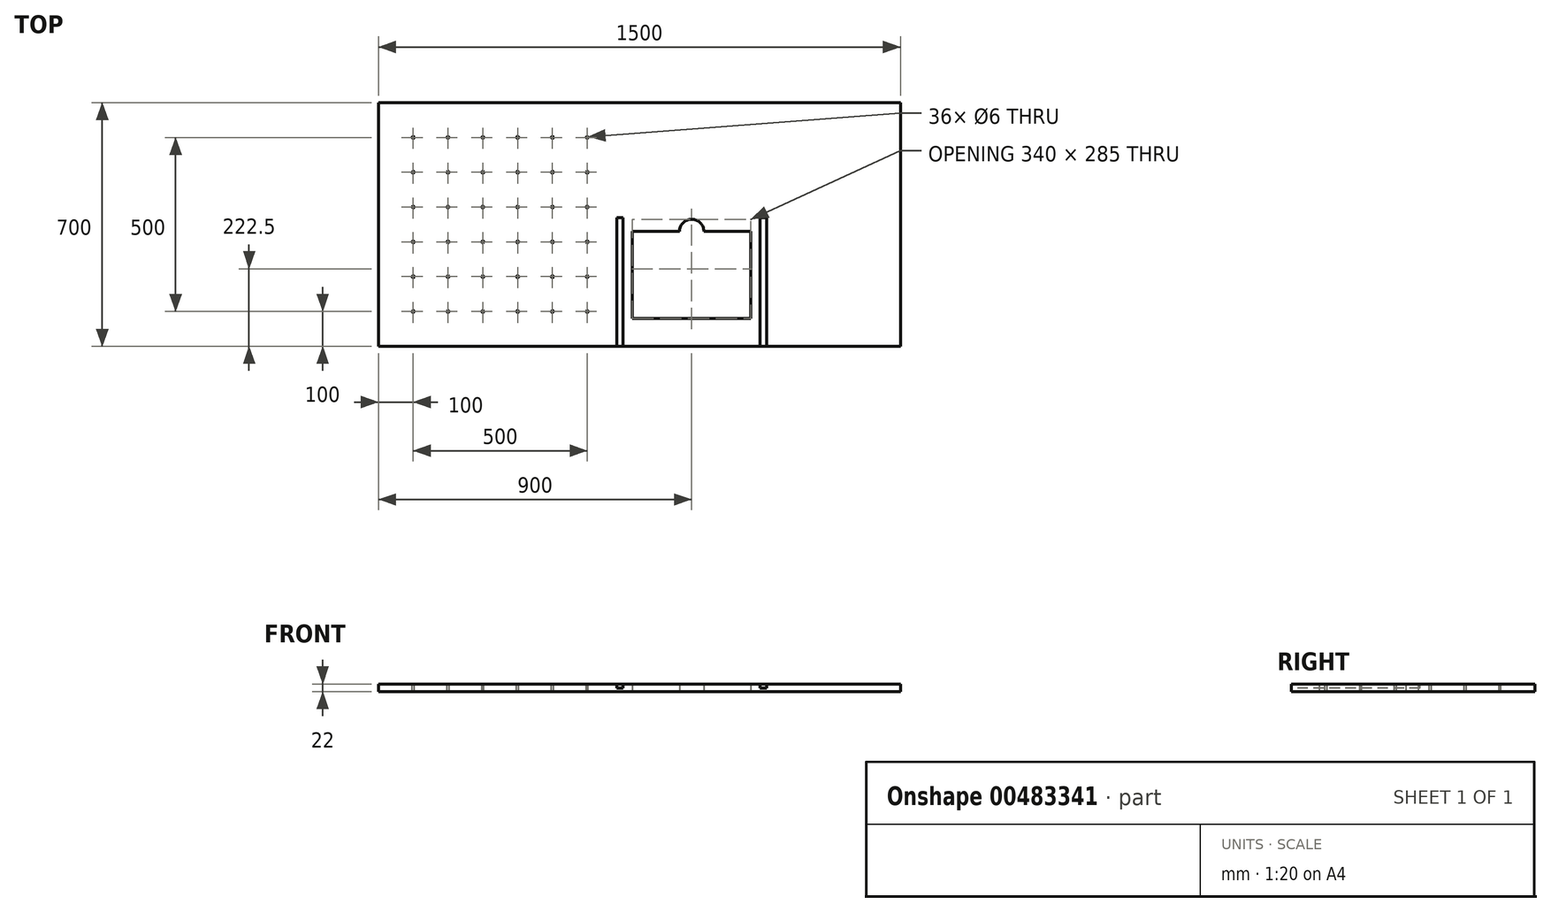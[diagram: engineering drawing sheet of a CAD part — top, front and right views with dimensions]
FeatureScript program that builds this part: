
annotation { "Feature Type Name" : "Feature", "Feature Type Description" : "" }
export const myFeature = defineFeature(function(context is Context, id is Id, definition is map)
    precondition{}
    {
        {
            var Q0;
            Q0=qCreatedBy(makeId("Top.planeOp"),FACE);
            var sketch = newSketch(context, id + "F0", { "sketchPlane" : qUnion([Q0])});
            skLineSegment(sketch, "E0.bottom", {"start": v(750, 350) * mm, "end": v(-750, 350) * mm});
            skLineSegment(sketch, "E0.top", {"start": v(750, -350) * mm, "end": v(-750, -350) * mm});
            skLineSegment(sketch, "E0.left", {"start": v(750, 350) * mm, "end": v(750, -350) * mm});
            skLineSegment(sketch, "E0.right", {"start": v(-750, 350) * mm, "end": v(-750, -350) * mm});
            skPoint(sketch, "E0.middle", {"position": v(0, 0) * mm});
            skLineSegment(sketch, "E1", {"start": v(150, 350) * mm, "end": v(150, -350) * mm, "construction": true});
            skLineSegment(sketch, "E2", {"start": v(150, 83.34) * mm, "end": v(750, 83.34) * mm, "construction": true});
            skLineSegment(sketch, "E3", {"start": v(150, -270) * mm, "end": v(750, -270) * mm, "construction": true});
            skLineSegment(sketch, "E4.0", {"start": v(150, -145) * mm, "end": v(750, -145) * mm, "construction": true});
            skLineSegment(sketch, "E5.bottom", {"start": v(320, -20) * mm, "end": v(185, -20) * mm});
            skLineSegment(sketch, "E5.top", {"start": v(320, -270) * mm, "end": v(-20, -270) * mm});
            skLineSegment(sketch, "E5.left", {"start": v(320, -20) * mm, "end": v(320, -270) * mm});
            skLineSegment(sketch, "E5.right", {"start": v(-20, -20) * mm, "end": v(-20, -270) * mm});
            skPoint(sketch, "E5.middle", {"position": v(150, -145) * mm});
            skArc(sketch, "E6", {"start": v(185, -20) * mm, "mid": v(150, 15) * mm, "end": v(115, -20) * mm});
            skLineSegment(sketch, "E7.trimOffspring", {"start": v(115, -20) * mm, "end": v(-20, -20) * mm});
            skSolve(sketch);
        }
        {
            var Q0;
            Q0=makeQuery(id+"F0.imprint","IMPRINT",FACE,{"disambiguationData":[TD([[makeQuery(id+"F0.imprint","IMPRINT",EDGE,{"derivedFrom":sQuery(id+"F0.wireOp",EDGE,"E0.bottom")}),1.0]])]});
            extrude(context, id + "F1", {"entities" : qUnion([Q0]), "depth" : 22 * mm});
        }
        {
            var Q0;
            Q0=makeQuery(id+"F1.opExtrude","SWEPT_FACE",FACE,{"disambiguationData":[OSD([sQuery(id+"F0.wireOp",EDGE,"E0.top")])]});
            var sketch = newSketch(context, id + "F2", { "sketchPlane" : qUnion([Q0])});
            skLineSegment(sketch, "E8", {"start": v(-65.47, 22) * mm, "end": v(-65.47, 10) * mm});
            skLineSegment(sketch, "E9", {"start": v(-65.47, 10) * mm, "end": v(-46.62, 10) * mm});
            skLineSegment(sketch, "E10", {"start": v(-46.62, 10) * mm, "end": v(-46.62, 22) * mm});
            skLineSegment(sketch, "E11", {"start": v(-46.62, 22) * mm, "end": v(-65.47, 22) * mm});
            skPoint(sketch, "E12.0", {"position": v(150, 22) * mm});
            skLineSegment(sketch, "E13", {"start": v(150, 22) * mm, "end": v(150, 0) * mm, "construction": true});
            skLineSegment(sketch, "E14.MirrorCS", {"start": v(346.62, 10) * mm, "end": v(346.62, 22) * mm});
            skLineSegment(sketch, "E15.MirrorCS", {"start": v(365.47, 10) * mm, "end": v(346.62, 10) * mm});
            skLineSegment(sketch, "E16.MirrorCS", {"start": v(365.47, 22) * mm, "end": v(365.47, 10) * mm});
            skLineSegment(sketch, "E17.MirrorCS", {"start": v(346.62, 22) * mm, "end": v(365.47, 22) * mm});
            skSolve(sketch);
        }
        {
            var Q0;
            Q0=makeQuery(id+"F2.imprint","IMPRINT",FACE,{"disambiguationData":[TD([[makeQuery(id+"F2.imprint","IMPRINT",EDGE,{"derivedFrom":sQuery(id+"F2.wireOp",EDGE,"E8")}),1.0]])]});
            var Q1;
            Q1=makeQuery(id+"F2.imprint","IMPRINT",FACE,{"disambiguationData":[TD([[makeQuery(id+"F2.imprint","IMPRINT",EDGE,{"derivedFrom":sQuery(id+"F2.wireOp",EDGE,"E14.MirrorCS")}),-1.0]])]});
            extrude(context, id + "F3", {"entities" : qUnion([Q0, Q1]), "operationType" : NewBodyOperationType.REMOVE, "oppositeDirection" : true, "depth" : 370 * mm});
        }
        {
            var Q0;
            Q0=makeQuery(id+"F1.opExtrude","CAP_FACE",FACE,{"disambiguationData":[OSD([sQuery(id+"F0.wireOp",EDGE,"E0.bottom"),sQuery(id+"F0.wireOp",EDGE,"E0.top"),sQuery(id+"F0.wireOp",EDGE,"E0.left"),sQuery(id+"F0.wireOp",EDGE,"E0.right"),sQuery(id+"F0.wireOp",EDGE,"E5.bottom"),sQuery(id+"F0.wireOp",EDGE,"E5.top"),sQuery(id+"F0.wireOp",EDGE,"E5.left"),sQuery(id+"F0.wireOp",EDGE,"E5.right"),sQuery(id+"F0.wireOp",EDGE,"E6"),sQuery(id+"F0.wireOp",EDGE,"E7.trimOffspring")])],"isStart":false});
            var sketch = newSketch(context, id + "F4", { "sketchPlane" : qUnion([Q0])});
            skPoint(sketch, "E18", {"position": v(-650, -250) * mm});
            skPoint(sketch, "E19.0.1.0", {"position": v(-650, -150) * mm});
            skPoint(sketch, "E19.0.2.0", {"position": v(-650, -50) * mm});
            skPoint(sketch, "E19.0.3.0", {"position": v(-650, 50) * mm});
            skPoint(sketch, "E19.0.4.0", {"position": v(-650, 150) * mm});
            skPoint(sketch, "E19.0.5.0", {"position": v(-650, 250) * mm});
            skPoint(sketch, "E19.1.0.0", {"position": v(-550, -250) * mm});
            skPoint(sketch, "E19.1.1.0", {"position": v(-550, -150) * mm});
            skPoint(sketch, "E19.1.2.0", {"position": v(-550, -50) * mm});
            skPoint(sketch, "E19.1.3.0", {"position": v(-550, 50) * mm});
            skPoint(sketch, "E19.1.4.0", {"position": v(-550, 150) * mm});
            skPoint(sketch, "E19.1.5.0", {"position": v(-550, 250) * mm});
            skPoint(sketch, "E19.2.0.0", {"position": v(-450, -250) * mm});
            skPoint(sketch, "E19.2.1.0", {"position": v(-450, -150) * mm});
            skPoint(sketch, "E19.2.2.0", {"position": v(-450, -50) * mm});
            skPoint(sketch, "E19.2.3.0", {"position": v(-450, 50) * mm});
            skPoint(sketch, "E19.2.4.0", {"position": v(-450, 150) * mm});
            skPoint(sketch, "E19.2.5.0", {"position": v(-450, 250) * mm});
            skPoint(sketch, "E19.3.0.0", {"position": v(-350, -250) * mm});
            skPoint(sketch, "E19.3.1.0", {"position": v(-350, -150) * mm});
            skPoint(sketch, "E19.3.2.0", {"position": v(-350, -50) * mm});
            skPoint(sketch, "E19.3.3.0", {"position": v(-350, 50) * mm});
            skPoint(sketch, "E19.3.4.0", {"position": v(-350, 150) * mm});
            skPoint(sketch, "E19.3.5.0", {"position": v(-350, 250) * mm});
            skPoint(sketch, "E19.4.0.0", {"position": v(-250, -250) * mm});
            skPoint(sketch, "E19.4.1.0", {"position": v(-250, -150) * mm});
            skPoint(sketch, "E19.4.2.0", {"position": v(-250, -50) * mm});
            skPoint(sketch, "E19.4.3.0", {"position": v(-250, 50) * mm});
            skPoint(sketch, "E19.4.4.0", {"position": v(-250, 150) * mm});
            skPoint(sketch, "E19.4.5.0", {"position": v(-250, 250) * mm});
            skPoint(sketch, "E19.5.0.0", {"position": v(-150, -250) * mm});
            skPoint(sketch, "E19.5.1.0", {"position": v(-150, -150) * mm});
            skPoint(sketch, "E19.5.2.0", {"position": v(-150, -50) * mm});
            skPoint(sketch, "E19.5.3.0", {"position": v(-150, 50) * mm});
            skPoint(sketch, "E19.5.4.0", {"position": v(-150, 150) * mm});
            skPoint(sketch, "E19.5.5.0", {"position": v(-150, 250) * mm});
            skLineSegment(sketch, "E19.direction1", {"start": v(-650, -250) * mm, "end": v(-550, -250) * mm, "construction": true});
            skLineSegment(sketch, "E19.direction2", {"start": v(-650, -250) * mm, "end": v(-650, -150) * mm, "construction": true});
            skSolve(sketch);
        }
        {
            var Q0;
            Q0=sQuery(id+"F4.wireOp",VERTEX,"E18");
            var Q1;
            Q1=sQuery(id+"F4.wireOp",VERTEX,"E19.1.0.0");
            var Q2;
            Q2=sQuery(id+"F4.wireOp",VERTEX,"E19.2.0.0");
            var Q3;
            Q3=sQuery(id+"F4.wireOp",VERTEX,"E19.0.1.0");
            var Q4;
            Q4=sQuery(id+"F4.wireOp",VERTEX,"E19.1.1.0");
            var Q5;
            Q5=sQuery(id+"F4.wireOp",VERTEX,"E19.2.1.0");
            var Q6;
            Q6=sQuery(id+"F4.wireOp",VERTEX,"E19.3.1.0");
            var Q7;
            Q7=sQuery(id+"F4.wireOp",VERTEX,"E19.4.1.0");
            var Q8;
            Q8=sQuery(id+"F4.wireOp",VERTEX,"E19.5.1.0");
            var Q9;
            Q9=sQuery(id+"F4.wireOp",VERTEX,"E19.5.0.0");
            var Q10;
            Q10=sQuery(id+"F4.wireOp",VERTEX,"E19.3.0.0");
            var Q11;
            Q11=sQuery(id+"F4.wireOp",VERTEX,"E19.4.0.0");
            var Q12;
            Q12=sQuery(id+"F4.wireOp",VERTEX,"E19.0.2.0");
            var Q13;
            Q13=sQuery(id+"F4.wireOp",VERTEX,"E19.0.3.0");
            var Q14;
            Q14=sQuery(id+"F4.wireOp",VERTEX,"E19.0.4.0");
            var Q15;
            Q15=sQuery(id+"F4.wireOp",VERTEX,"E19.0.5.0");
            var Q16;
            Q16=sQuery(id+"F4.wireOp",VERTEX,"E19.1.5.0");
            var Q17;
            Q17=sQuery(id+"F4.wireOp",VERTEX,"E19.1.4.0");
            var Q18;
            Q18=sQuery(id+"F4.wireOp",VERTEX,"E19.1.3.0");
            var Q19;
            Q19=sQuery(id+"F4.wireOp",VERTEX,"E19.1.2.0");
            var Q20;
            Q20=sQuery(id+"F4.wireOp",VERTEX,"E19.2.2.0");
            var Q21;
            Q21=sQuery(id+"F4.wireOp",VERTEX,"E19.2.3.0");
            var Q22;
            Q22=sQuery(id+"F4.wireOp",VERTEX,"E19.2.4.0");
            var Q23;
            Q23=sQuery(id+"F4.wireOp",VERTEX,"E19.2.5.0");
            var Q24;
            Q24=sQuery(id+"F4.wireOp",VERTEX,"E19.3.5.0");
            var Q25;
            Q25=sQuery(id+"F4.wireOp",VERTEX,"E19.4.5.0");
            var Q26;
            Q26=sQuery(id+"F4.wireOp",VERTEX,"E19.5.5.0");
            var Q27;
            Q27=sQuery(id+"F4.wireOp",VERTEX,"E19.3.4.0");
            var Q28;
            Q28=sQuery(id+"F4.wireOp",VERTEX,"E19.3.3.0");
            var Q29;
            Q29=sQuery(id+"F4.wireOp",VERTEX,"E19.3.2.0");
            var Q30;
            Q30=sQuery(id+"F4.wireOp",VERTEX,"E19.4.3.0");
            var Q31;
            Q31=sQuery(id+"F4.wireOp",VERTEX,"E19.4.4.0");
            var Q32;
            Q32=sQuery(id+"F4.wireOp",VERTEX,"E19.5.3.0");
            var Q33;
            Q33=sQuery(id+"F4.wireOp",VERTEX,"E19.4.2.0");
            var Q34;
            Q34=sQuery(id+"F4.wireOp",VERTEX,"E19.5.2.0");
            var Q35;
            Q35=sQuery(id+"F4.wireOp",VERTEX,"E19.5.4.0");
            var Q36;
            Q36=makeQuery(id+"F1.opExtrude","SWEPT_BODY",BODY,{"disambiguationData":[OSD([sQuery(id+"F0.wireOp",EDGE,"E0.bottom"),sQuery(id+"F0.wireOp",EDGE,"E0.top"),sQuery(id+"F0.wireOp",EDGE,"E0.left"),sQuery(id+"F0.wireOp",EDGE,"E0.right"),sQuery(id+"F0.wireOp",EDGE,"E5.bottom"),sQuery(id+"F0.wireOp",EDGE,"E5.top"),sQuery(id+"F0.wireOp",EDGE,"E5.left"),sQuery(id+"F0.wireOp",EDGE,"E5.right"),sQuery(id+"F0.wireOp",EDGE,"E6"),sQuery(id+"F0.wireOp",EDGE,"E7.trimOffspring")])]});
            hole(context, id + "F5", {"style" : HoleStyle.SIMPLE, "endStyle" : HoleEndStyle.THROUGH, "holeDiameter" : 6 * mm, "tappedDepth" : 21 * mm, "tapClearance" : 3, "startFromSketch" : true, "locations" : qUnion([Q0, Q1, Q2, Q3, Q4, Q5, Q6, Q7, Q8, Q9, Q10, Q11, Q12, Q13, Q14, Q15, Q16, Q17, Q18, Q19, Q20, Q21, Q22, Q23, Q24, Q25, Q26, Q27, Q28, Q29, Q30, Q31, Q32, Q33, Q34, Q35]), "scope" : qUnion([Q36])});
        }
    });
